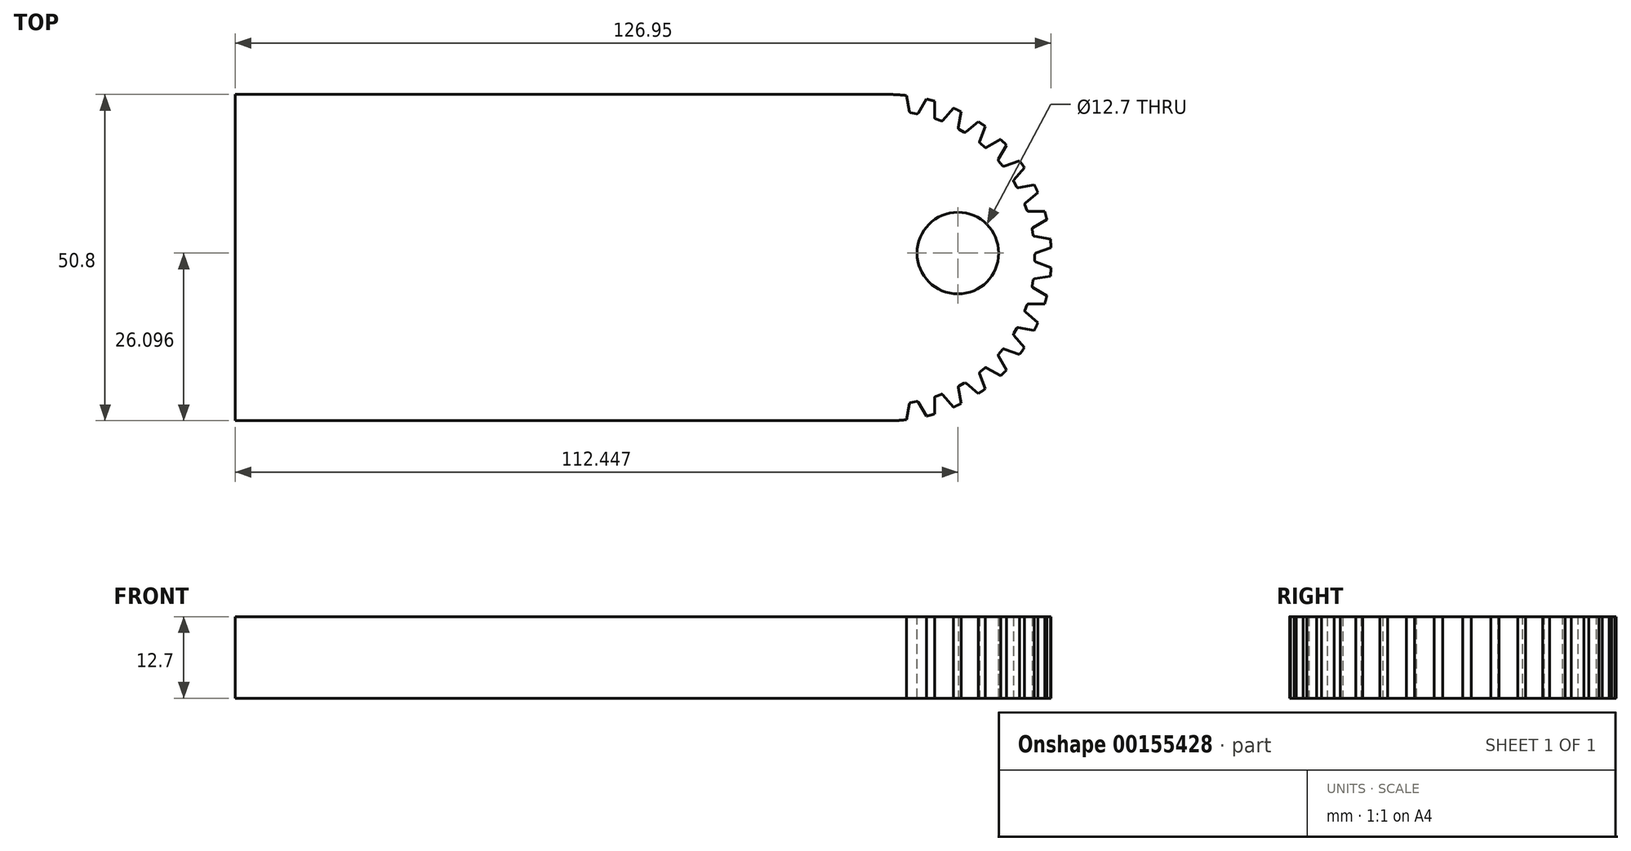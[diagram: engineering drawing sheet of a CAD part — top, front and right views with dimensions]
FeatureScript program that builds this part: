
annotation { "Feature Type Name" : "Feature", "Feature Type Description" : "" }
export const myFeature = defineFeature(function(context is Context, id is Id, definition is map)
    precondition{}
    {
        {
            var Q0;
            Q0=qCreatedBy(makeId("Top.planeOp"),FACE);
            var sketch = newSketch(context, id + "F0", { "sketchPlane" : qUnion([Q0])});
            skLineSegment(sketch, "E0.bottom", {"start": v(0, 0) * mm, "end": v(-127, 0) * mm});
            skLineSegment(sketch, "E0.top", {"start": v(0, -50.8) * mm, "end": v(-127, -50.8) * mm});
            skLineSegment(sketch, "E0.left", {"start": v(0, 0) * mm, "end": v(0, -50.8) * mm});
            skLineSegment(sketch, "E0.right", {"start": v(-127, 0) * mm, "end": v(-127, -50.8) * mm});
            skSolve(sketch);
        }
        {
            var Q0;
            Q0=makeQuery(id+"F0.imprint","IMPRINT",FACE,{"disambiguationData":[TD([[makeQuery(id+"F0.imprint","IMPRINT",EDGE,{"derivedFrom":sQuery(id+"F0.wireOp",EDGE,"E0.bottom")}),1.0]])]});
            extrude(context, id + "F1", {"entities" : qUnion([Q0]), "depth" : 12.7 * mm});
        }
        {
            var Q0;
            Q0=makeQuery(id+"F1.opExtrude","SWEPT_EDGE",EDGE,{"disambiguationData":[OSD([sQuery(id+"F0.wireOp",EDGE,"E0.top"),sQuery(id+"F0.wireOp",EDGE,"E0.left")])]});
            var Q1;
            Q1=makeQuery(id+"F1.opExtrude","SWEPT_EDGE",EDGE,{"disambiguationData":[OSD([sQuery(id+"F0.wireOp",EDGE,"E0.bottom"),sQuery(id+"F0.wireOp",EDGE,"E0.left")])]});
            fillet(context, id + "F2", {"entities" : qUnion([Q0, Q1]), "radius" : 25.4 * mm, "tangentPropagation" : true, "allowEdgeOverflow" : false});
        }
        {
            var Q0;
            Q0=makeQuery(id+"F1.opExtrude","CAP_FACE",FACE,{"disambiguationData":[OSD([sQuery(id+"F0.wireOp",EDGE,"E0.bottom"),sQuery(id+"F0.wireOp",EDGE,"E0.top"),sQuery(id+"F0.wireOp",EDGE,"E0.left"),sQuery(id+"F0.wireOp",EDGE,"E0.right")])],"isStart":false});
            var sketch = newSketch(context, id + "F3", { "sketchPlane" : qUnion([Q0])});
            skPoint(sketch, "E1", {"position": v(-25.4, -25.4) * mm});
            skLineSegment(sketch, "E2", {"start": v(-25.4, -25.4) * mm, "end": v(0, -25.4) * mm, "construction": true});
            skLineSegment(sketch, "E3", {"start": v(-0.05, -26.96) * mm, "end": v(-2.58, -26.04) * mm});
            skLineSegment(sketch, "E4.MirrorCS", {"start": v(-0.05, -23.84) * mm, "end": v(-2.58, -24.76) * mm});
            skLineSegment(sketch, "E5", {"start": v(-2.58, -24.76) * mm, "end": v(-2.58, -26.04) * mm});
            skSolve(sketch);
        }
        {
            var Q0;
            {var subQ0=sQuery(id+"F3.wireOp",EDGE,"E3");Q0=makeQuery(id+"F3.imprint","IMPRINT",FACE,{"disambiguationData":[TD([[makeQuery(id+"F3.imprint","IMPRINT",EDGE,{"derivedFrom":subQ0}),-1.0]])]});}
            extrude(context, id + "F4", {"entities" : qUnion([Q0]), "operationType" : NewBodyOperationType.REMOVE, "oppositeDirection" : true, "depth" : 25.4 * mm});
        }
        {
            var Q0;
            Q0=makeQuery(id+"F4.boolean.opBoolean","COPY",EDGE,{"derivedFrom":makeQuery(id+"F4.opExtrude","SWEPT_EDGE",EDGE,{"disambiguationData":[OSD([sQuery(id+"F3.wireOp",EDGE,"E3"),sQuery(id+"F3.wireOp",EDGE,"E5")])]})});
            var Q1;
            Q1=makeQuery(id+"F4.boolean.opBoolean","COPY",EDGE,{"derivedFrom":makeQuery(id+"F4.opExtrude","SWEPT_EDGE",EDGE,{"disambiguationData":[OSD([sQuery(id+"F3.wireOp",EDGE,"E4.MirrorCS"),sQuery(id+"F3.wireOp",EDGE,"E5")])]})});
            fillet(context, id + "F5", {"entities" : qUnion([Q0, Q1]), "radius" : 0.25 * mm, "tangentPropagation" : true, "allowEdgeOverflow" : false});
        }
        {
            var Q0;
            Q0=makeQuery(id+"F4.boolean.opBoolean","COPY",FACE,{"derivedFrom":makeQuery(id+"F4.opExtrude","SWEPT_FACE",FACE,{"disambiguationData":[OSD([sQuery(id+"F3.wireOp",EDGE,"E3")])]})});
            var Q1;
            Q1=makeQuery(id+"F5.opFillet","BLEND_FACE",FACE,{"disambiguationData":[OSD([sQuery(id+"F3.wireOp",EDGE,"E3"),sQuery(id+"F3.wireOp",EDGE,"E5")])]});
            var Q2;
            Q2=makeQuery(id+"F4.boolean.opBoolean","COPY",FACE,{"derivedFrom":makeQuery(id+"F4.opExtrude","SWEPT_FACE",FACE,{"disambiguationData":[OSD([sQuery(id+"F3.wireOp",EDGE,"E5")])]})});
            var Q3;
            Q3=makeQuery(id+"F5.opFillet","BLEND_FACE",FACE,{"disambiguationData":[OSD([sQuery(id+"F3.wireOp",EDGE,"E4.MirrorCS"),sQuery(id+"F3.wireOp",EDGE,"E5")])]});
            var Q4;
            Q4=makeQuery(id+"F4.boolean.opBoolean","COPY",FACE,{"derivedFrom":makeQuery(id+"F4.opExtrude","SWEPT_FACE",FACE,{"disambiguationData":[OSD([sQuery(id+"F3.wireOp",EDGE,"E4.MirrorCS")])]})});
            var Q5;
            {var subQ1=sQuery(id+"F0.wireOp",EDGE,"E0.left");var subQ2=sQuery(id+"F0.wireOp",EDGE,"E0.top");Q5=makeQuery(id+"F4.boolean.opBoolean","SPLIT",FACE,{"disambiguationData":[TD([makeQuery(id+"F1.opExtrude","SWEPT_FACE",FACE,{"disambiguationData":[OSD([subQ2])]})])],"derivedFrom":makeQuery(id+"F2.opFillet","BLEND_FACE",FACE,{"disambiguationData":[OSD([subQ2,subQ1])]})});}
            circularPattern(context, id + "F6", {"patternType" : PatternType.FACE, "faces" : qUnion([Q0, Q1, Q2, Q3, Q4]), "axis" : qUnion([Q5]), "angle" : 10 * degree, "instanceCount" : 9});
        }
        {
            var Q0;
            Q0=makeQuery(id+"F4.boolean.opBoolean","COPY",FACE,{"derivedFrom":makeQuery(id+"F4.opExtrude","SWEPT_FACE",FACE,{"disambiguationData":[OSD([sQuery(id+"F3.wireOp",EDGE,"E4.MirrorCS")])]})});
            var Q1;
            Q1=makeQuery(id+"F5.opFillet","BLEND_FACE",FACE,{"disambiguationData":[OSD([sQuery(id+"F3.wireOp",EDGE,"E4.MirrorCS"),sQuery(id+"F3.wireOp",EDGE,"E5")])]});
            var Q2;
            Q2=makeQuery(id+"F5.opFillet","BLEND_FACE",FACE,{"disambiguationData":[OSD([sQuery(id+"F3.wireOp",EDGE,"E3"),sQuery(id+"F3.wireOp",EDGE,"E5")])]});
            var Q3;
            Q3=makeQuery(id+"F4.boolean.opBoolean","COPY",FACE,{"derivedFrom":makeQuery(id+"F4.opExtrude","SWEPT_FACE",FACE,{"disambiguationData":[OSD([sQuery(id+"F3.wireOp",EDGE,"E5")])]})});
            var Q4;
            Q4=makeQuery(id+"F4.boolean.opBoolean","COPY",FACE,{"derivedFrom":makeQuery(id+"F4.opExtrude","SWEPT_FACE",FACE,{"disambiguationData":[OSD([sQuery(id+"F3.wireOp",EDGE,"E3")])]})});
            var Q5;
            {var subQ0=sQuery(id+"F0.wireOp",EDGE,"E0.bottom");var subQ2=sQuery(id+"F0.wireOp",EDGE,"E0.left");var subQ3=sQuery(id+"F0.wireOp",EDGE,"E0.top");Q5=makeQuery(id+"F4.boolean.opBoolean","SPLIT",FACE,{"disambiguationData":[TD([makeQuery(id+"F1.opExtrude","SWEPT_FACE",FACE,{"disambiguationData":[OSD([subQ0])]})])],"derivedFrom":makeQuery(id+"F2.opFillet","BLEND_FACE",FACE,{"disambiguationData":[OSD([subQ3,subQ2])]})});}
            circularPattern(context, id + "F7", {"patternType" : PatternType.FACE, "faces" : qUnion([Q0, Q1, Q2, Q3, Q4]), "axis" : qUnion([Q5]), "angle" : 10 * degree, "instanceCount" : 9, "oppositeDirection" : true});
        }
        {
            var Q0;
            Q0=makeQuery(id+"F1.opExtrude","CAP_FACE",FACE,{"disambiguationData":[OSD([sQuery(id+"F0.wireOp",EDGE,"E0.bottom"),sQuery(id+"F0.wireOp",EDGE,"E0.top"),sQuery(id+"F0.wireOp",EDGE,"E0.left"),sQuery(id+"F0.wireOp",EDGE,"E0.right")])],"isStart":false});
            var sketch = newSketch(context, id + "F8", { "sketchPlane" : qUnion([Q0])});
            skPoint(sketch, "E6", {"position": v(-10.3, -24.7) * mm});
            skPoint(sketch, "E7", {"position": v(-22.53, -24.7) * mm});
            skCircle(sketch, "E8", {"center": v(-22.53, -24.7) * mm, "radius": 3.18 * mm});
            skPoint(sketch, "E9", {"position": v(-25.7, -24.7) * mm});
            skPoint(sketch, "E10", {"position": v(-19.35, -24.7) * mm});
            skPoint(sketch, "E11", {"position": v(-18, -24.7) * mm});
            skLineSegment(sketch, "E12", {"start": v(-22.53, -24.7) * mm, "end": v(-1.23, -24.7) * mm});
            skPoint(sketch, "E12.endSnap0", {"position": v(-1.23, -24.27) * mm});
            skLineSegment(sketch, "E13", {"start": v(-1.23, -24.7) * mm, "end": v(-13.93, -24.7) * mm});
            skPoint(sketch, "E14", {"position": v(-13.15, -24.7) * mm});
            skPoint(sketch, "E15", {"position": v(-14.55, -24.7) * mm});
            skSolve(sketch);
        }
        {
            var Q0;
            Q0=sQuery(id+"F8.wireOp",VERTEX,"E15");
            var Q1;
            Q1=makeQuery(id+"F1.opExtrude","SWEPT_BODY",BODY,{"disambiguationData":[OSD([sQuery(id+"F0.wireOp",EDGE,"E0.bottom"),sQuery(id+"F0.wireOp",EDGE,"E0.top"),sQuery(id+"F0.wireOp",EDGE,"E0.left"),sQuery(id+"F0.wireOp",EDGE,"E0.right")])]});
            hole(context, id + "F9", {"style" : HoleStyle.SIMPLE, "endStyle" : HoleEndStyle.BLIND, "holeDiameter" : 12.7 * mm, "holeDepth" : 12.7 * mm, "locations" : qUnion([Q0]), "scope" : qUnion([Q1])});
        }
    });
